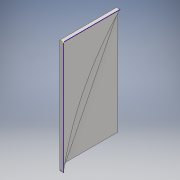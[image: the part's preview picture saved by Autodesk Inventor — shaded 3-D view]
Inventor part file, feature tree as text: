
AUTODESK INVENTOR PART (.ipt)
format: ipt  version: 2018 (Build 220112000, 112)  size: 128,000 bytes
history: native  units: mm
features: sketch x6, extrude x4
ambient origin geometry x8: Origin, YZ Plane, XZ Plane, XY Plane, X Axis, Y Axis, Z Axis, Center Point
bodies: Solid1 (feature_tree)
feature tree (10):
  extrude  "Extrusion1"  Depth=10.0mm
  sketch  "Sketch2"  dims[d2=10.0mm d3=1000.0mm]
  extrude  "Extrusion2"  Depth=10.0mm
  sketch  "Sketch4"  dims[d8=50.0mm d9=50.0mm]
  extrude  "Extrusion3"  Depth=10.0mm TaperAngle=0.0deg
  extrude  "Extrusion4"  Depth=50.0mm
  sketch  "Sketch1"  dims[d0=500.0mm d1=10.0mm]
  sketch  "Sketch3"  dims[d4=10.0mm d5=0.0mm d6=10.0mm d7=0.0mm]
  sketch  "Sketch5"  dims[d10=51.0mm]
  sketch  "Sketch6"  dims[d11=10.0mm d12=0.0mm d13=10.0mm d14=0.0mm]
